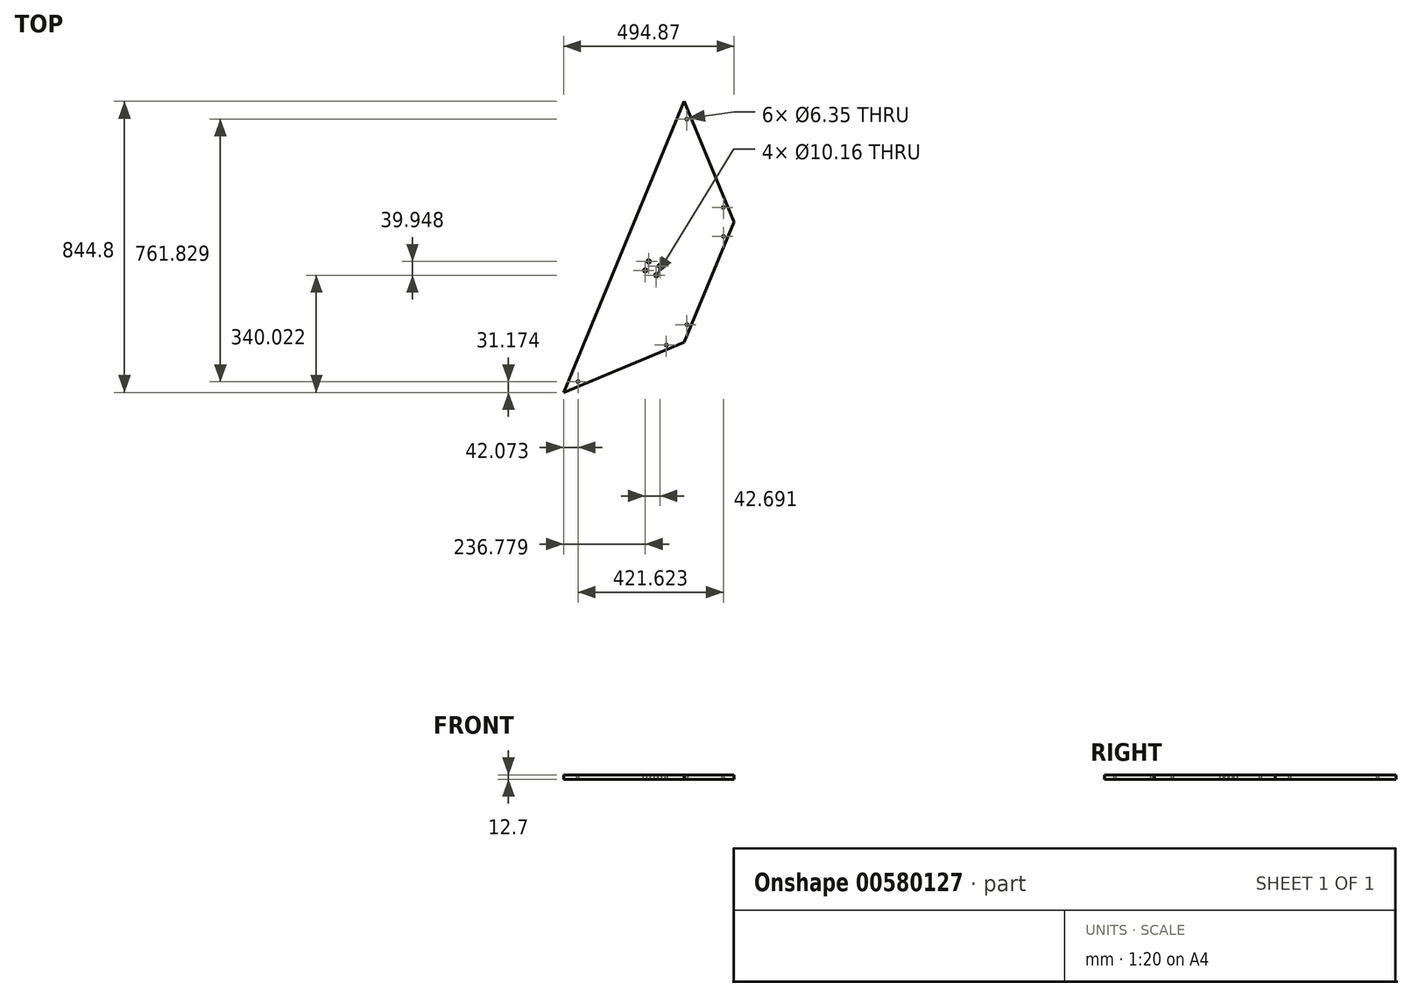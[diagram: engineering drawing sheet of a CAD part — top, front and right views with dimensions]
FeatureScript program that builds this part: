
annotation { "Feature Type Name" : "Feature", "Feature Type Description" : "" }
export const myFeature = defineFeature(function(context is Context, id is Id, definition is map)
    precondition{}
    {
        {
            var Q0;
            Q0=qCreatedBy(makeId("Top.planeOp"),FACE);
            var sketch = newSketch(context, id + "F0", { "sketchPlane" : qUnion([Q0])});
            skCircle(sketch, "E0.cCircle", {"center": v(0, 0) * mm, "radius": 494.87 * mm, "construction": true});
            skLineSegment(sketch, "E0.0", {"start": v(494.87, 0) * mm, "end": v(349.93, -349.93) * mm});
            skLineSegment(sketch, "E0.1", {"start": v(349.93, -349.93) * mm, "end": v(0, -494.87) * mm});
            skLineSegment(sketch, "E0.2", {"start": v(0, -494.87) * mm, "end": v(-349.93, -349.93) * mm});
            skLineSegment(sketch, "E0.3", {"start": v(-349.93, -349.93) * mm, "end": v(-494.87, 0) * mm});
            skLineSegment(sketch, "E0.4", {"start": v(-494.87, 0) * mm, "end": v(-349.93, 349.93) * mm});
            skLineSegment(sketch, "E0.5", {"start": v(-349.93, 349.93) * mm, "end": v(0, 494.87) * mm});
            skLineSegment(sketch, "E0.6", {"start": v(0, 494.87) * mm, "end": v(349.93, 349.93) * mm});
            skLineSegment(sketch, "E0.7", {"start": v(349.93, 349.93) * mm, "end": v(494.87, 0) * mm});
            skLineSegment(sketch, "E1", {"start": v(349.93, 349.93) * mm, "end": v(0, -494.87) * mm});
            skSolve(sketch);
        }
        {
            var Q0;
            Q0=makeQuery(id+"F0.imprint","IMPRINT",FACE,{"disambiguationData":[TD([[makeQuery(id+"F0.imprint","IMPRINT",EDGE,{"derivedFrom":sQuery(id+"F0.wireOp",EDGE,"E0.0")}),-1.0]])]});
            extrude(context, id + "F1", {"entities" : qUnion([Q0]), "depth" : 12.7 * mm, "offsetDistance" : 25.4 * mm});
        }
        {
            var Q0;
            Q0=makeQuery(id+"F1.opExtrude","CAP_FACE",FACE,{"disambiguationData":[OSD([sQuery(id+"F0.wireOp",EDGE,"E0.0"),sQuery(id+"F0.wireOp",EDGE,"E0.1"),sQuery(id+"F0.wireOp",EDGE,"E0.7"),sQuery(id+"F0.wireOp",EDGE,"E1")])],"isStart":false});
            var sketch = newSketch(context, id + "F2", { "sketchPlane" : qUnion([Q0])});
            skCircle(sketch, "E2", {"center": v(42.07, -463.7) * mm, "radius": 3.18 * mm});
            skCircle(sketch, "E3", {"center": v(298.13, -357.63) * mm, "radius": 3.17 * mm});
            skCircle(sketch, "E4", {"center": v(357.63, -298.13) * mm, "radius": 3.17 * mm});
            skCircle(sketch, "E5", {"center": v(463.7, -42.07) * mm, "radius": 3.17 * mm});
            skCircle(sketch, "E6", {"center": v(463.7, 42.07) * mm, "radius": 3.17 * mm});
            skCircle(sketch, "E7", {"center": v(357.63, 298.13) * mm, "radius": 3.18 * mm});
            skLineSegment(sketch, "E8", {"start": v(357.63, 298.13) * mm, "end": v(360.57, 299.35) * mm});
            skLineSegment(sketch, "E9", {"start": v(360.57, 299.35) * mm, "end": v(369.37, 303) * mm});
            skLineSegment(sketch, "E10", {"start": v(463.7, 42.07) * mm, "end": v(466.63, 43.29) * mm});
            skLineSegment(sketch, "E11", {"start": v(466.63, 43.29) * mm, "end": v(475.43, 46.93) * mm});
            skLineSegment(sketch, "E12", {"start": v(463.7, -42.07) * mm, "end": v(460.76, -40.86) * mm});
            skLineSegment(sketch, "E13", {"start": v(298.13, -357.63) * mm, "end": v(299.35, -360.57) * mm});
            skLineSegment(sketch, "E14", {"start": v(299.35, -360.57) * mm, "end": v(303, -369.37) * mm});
            skLineSegment(sketch, "E15", {"start": v(42.07, -463.7) * mm, "end": v(43.29, -466.63) * mm});
            skLineSegment(sketch, "E16", {"start": v(43.29, -466.63) * mm, "end": v(46.93, -475.43) * mm});
            skLineSegment(sketch, "E17", {"start": v(357.63, -298.13) * mm, "end": v(354.7, -296.92) * mm});
            skLineSegment(sketch, "E18", {"start": v(354.7, -296.92) * mm, "end": v(369.37, -303) * mm});
            skLineSegment(sketch, "E19", {"start": v(463.7, -42.07) * mm, "end": v(475.43, -46.93) * mm});
            skSolve(sketch);
        }
        {
            var Q0;
            Q0=qSketchRegion(id+"F2",true);
            extrude(context, id + "F3", {"entities" : qUnion([Q0]), "operationType" : NewBodyOperationType.REMOVE, "endBound" : BoundingType.THROUGH_ALL, "oppositeDirection" : true, "depth" : 25.4 * mm, "offsetDistance" : 25.4 * mm});
        }
        {
            var Q0;
            Q0=makeQuery(id+"F1.opExtrude","CAP_FACE",FACE,{"disambiguationData":[OSD([sQuery(id+"F0.wireOp",EDGE,"E0.0"),sQuery(id+"F0.wireOp",EDGE,"E0.1"),sQuery(id+"F0.wireOp",EDGE,"E0.7"),sQuery(id+"F0.wireOp",EDGE,"E1")])],"isStart":false});
            var sketch = newSketch(context, id + "F4", { "sketchPlane" : qUnion([Q0])});
            skLineSegment(sketch, "E20", {"start": v(136.95, -178.1) * mm, "end": v(207.63, -7.45) * mm});
            skLineSegment(sketch, "E21", {"start": v(207.63, -7.45) * mm, "end": v(379.5, -78.64) * mm});
            skLineSegment(sketch, "E22", {"start": v(379.5, -78.64) * mm, "end": v(308.12, -250.97) * mm});
            skLineSegment(sketch, "E23", {"start": v(136.95, -178.1) * mm, "end": v(308.12, -250.97) * mm});
            skCircle(sketch, "E24", {"center": v(268.78, -154.85) * mm, "radius": 5.08 * mm});
            skCircle(sketch, "E25", {"center": v(236.78, -140.8) * mm, "radius": 5.08 * mm});
            skCircle(sketch, "E26", {"center": v(279.47, -128.06) * mm, "radius": 5.08 * mm});
            skCircle(sketch, "E27", {"center": v(246.83, -114.9) * mm, "radius": 5.08 * mm});
            skSolve(sketch);
        }
        {
            var Q0;
            Q0=makeQuery(id+"F4.imprint","IMPRINT",FACE,{"disambiguationData":[TD([[makeQuery(id+"F4.imprint","IMPRINT",EDGE,{"derivedFrom":sQuery(id+"F4.wireOp",EDGE,"E27")}),1.0]])]});
            var Q1;
            Q1=makeQuery(id+"F4.imprint","IMPRINT",FACE,{"disambiguationData":[TD([[makeQuery(id+"F4.imprint","IMPRINT",EDGE,{"derivedFrom":sQuery(id+"F4.wireOp",EDGE,"E26")}),1.0]])]});
            var Q2;
            Q2=makeQuery(id+"F4.imprint","IMPRINT",FACE,{"disambiguationData":[TD([[makeQuery(id+"F4.imprint","IMPRINT",EDGE,{"derivedFrom":sQuery(id+"F4.wireOp",EDGE,"E24")}),1.0]])]});
            var Q3;
            Q3=makeQuery(id+"F4.imprint","IMPRINT",FACE,{"disambiguationData":[TD([[makeQuery(id+"F4.imprint","IMPRINT",EDGE,{"derivedFrom":sQuery(id+"F4.wireOp",EDGE,"E25")}),1.0]])]});
            extrude(context, id + "F5", {"entities" : qUnion([Q0, Q1, Q2, Q3]), "operationType" : NewBodyOperationType.REMOVE, "oppositeDirection" : true, "depth" : 25.4 * mm, "offsetDistance" : 25.4 * mm});
        }
    });
